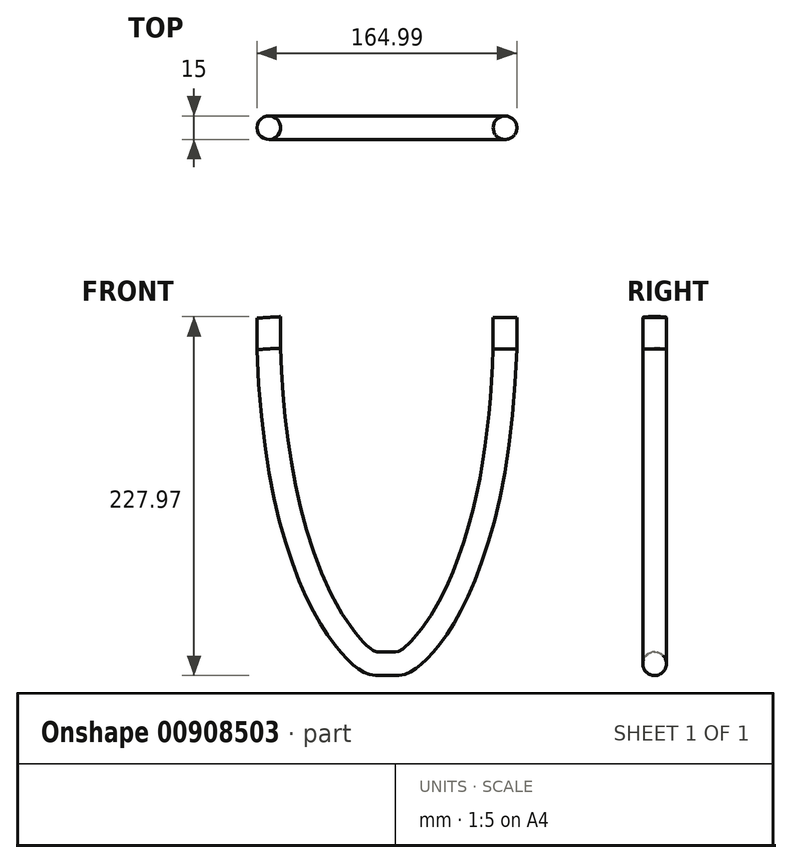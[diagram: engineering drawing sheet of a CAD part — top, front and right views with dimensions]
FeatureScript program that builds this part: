
annotation { "Feature Type Name" : "Feature", "Feature Type Description" : "" }
export const myFeature = defineFeature(function(context is Context, id is Id, definition is map)
    precondition{}
    {
        {
            var Q0;
            Q0=qCreatedBy(makeId("Front.planeOp"),FACE);
            var sketch = newSketch(context, id + "F0", { "sketchPlane" : qUnion([Q0])});
            skPoint(sketch, "E0", {"position": v(75, 0) * mm});
            skPoint(sketch, "E1", {"position": v(0, -200) * mm});
            skPoint(sketch, "E2.MirrorP", {"position": v(-75, 0) * mm});
            skPoint(sketch, "E3", {"position": v(12.8, -197.78) * mm});
            skFitSpline(sketch, "E4", {"points": [v(75, 0) * mm, v(12.8, -197.78) * mm, v(0, -200) * mm], "startDerivative": vector(-15.9, -511.27) * mm, "endDerivative": vector(-103.15, 0) * mm});
            skFitSpline(sketch, "E5.MirrorCS", {"points": [v(-75, 0) * mm, v(-12.8, -197.78) * mm, v(0, -200) * mm], "startDerivative": vector(15.9, -511.27) * mm, "endDerivative": vector(103.15, 0) * mm});
            skSolve(sketch);
        }
        {
            var Q0;
            Q0=qCreatedBy(makeId("Top.planeOp"),FACE);
            var sketch = newSketch(context, id + "F1", { "sketchPlane" : qUnion([Q0])});
            skCircle(sketch, "E6", {"center": v(75, 0) * mm, "radius": 7.5 * mm});
            skSolve(sketch);
        }
        {
            var Q0;
            Q0=makeQuery(id+"F1.imprint","IMPRINT",FACE,{"disambiguationData":[TD([[makeQuery(id+"F1.imprint","IMPRINT",EDGE,{"derivedFrom":sQuery(id+"F1.wireOp",EDGE,"E6")}),1.0]])]});
            var Q1;
            Q1=sQuery(id+"F0.wireOp",EDGE,"E4");
            var Q2;
            Q2=sQuery(id+"F0.wireOp",EDGE,"E5.MirrorCS");
            sweep(context, id + "F2", {"profiles" : qUnion([Q0]), "path" : qUnion([Q1, Q2])});
        }
        {
            var Q0;
            Q0=makeQuery(id+"F2.opSweep","CAP_FACE",FACE,{"disambiguationData":[OSD([sQuery(id+"F0.wireOp",VERTEX,"E4.start"),sQuery(id+"F1.wireOp",EDGE,"E6")])],"isStart":true});
            var Q1;
            Q1=makeQuery(id+"F2.opSweep","CAP_FACE",FACE,{"disambiguationData":[OSD([sQuery(id+"F0.wireOp",VERTEX,"E5.MirrorCS.start"),sQuery(id+"F1.wireOp",EDGE,"E6")])],"isStart":false});
            extrude(context, id + "F3", {"entities" : qUnion([Q0, Q1]), "operationType" : NewBodyOperationType.ADD, "depth" : 20 * mm, "offsetDistance" : 25 * mm});
        }
    });
